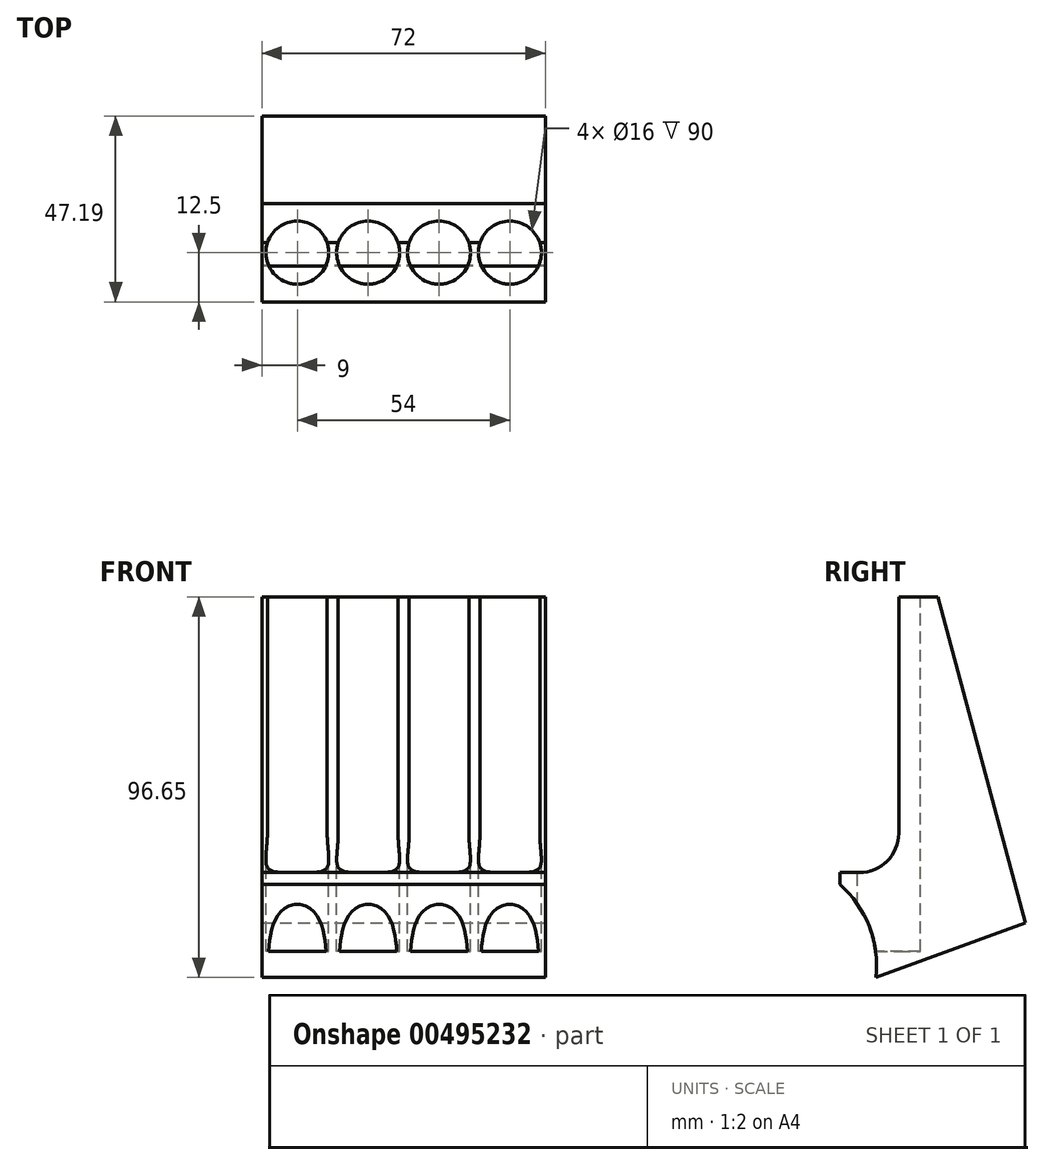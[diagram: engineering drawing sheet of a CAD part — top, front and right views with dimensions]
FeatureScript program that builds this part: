
annotation { "Feature Type Name" : "Feature", "Feature Type Description" : "" }
export const myFeature = defineFeature(function(context is Context, id is Id, definition is map)
    precondition{}
    {
        {
            var Q0;
            Q0=qCreatedBy(makeId("Front.planeOp"),FACE);
            var sketch = newSketch(context, id + "F0", { "sketchPlane" : qUnion([Q0])});
            skLineSegment(sketch, "E0.bottom", {"start": v(-36, 50) * mm, "end": v(36, 50) * mm});
            skLineSegment(sketch, "E0.top", {"start": v(-36, -50) * mm, "end": v(36, -50) * mm});
            skLineSegment(sketch, "E0.left", {"start": v(-36, 50) * mm, "end": v(-36, -50) * mm});
            skLineSegment(sketch, "E0.right", {"start": v(36, 50) * mm, "end": v(36, -50) * mm});
            skLineSegment(sketch, "E1", {"start": v(0, 50) * mm, "end": v(0, -50) * mm, "construction": true});
            skLineSegment(sketch, "E2", {"start": v(-20, 50) * mm, "end": v(-20, -50) * mm, "construction": true});
            skLineSegment(sketch, "E3", {"start": v(20, 50) * mm, "end": v(20, -50) * mm, "construction": true});
            skSolve(sketch);
        }
        {
            var Q0;
            Q0 = qSketchRegion(id + "F0", true);
            extrude(context, id + "F1", {"entities" : qUnion([Q0]), "oppositeDirection" : true, "depth" : 25 * mm, "offsetDistance" : 25 * mm});
        }
        {
            var Q0;
            Q0=makeQuery(id+"F1.opExtrude","SWEPT_FACE",FACE,{"disambiguationData":[OSD([sQuery(id+"F0.wireOp",EDGE,"E0.bottom")])]});
            var sketch = newSketch(context, id + "F2", { "sketchPlane" : qUnion([Q0])});
            skCircle(sketch, "E4", {"center": v(-27, 12.5) * mm, "radius": 8 * mm});
            skCircle(sketch, "E5", {"center": v(-9, 12.5) * mm, "radius": 8 * mm});
            skCircle(sketch, "E6", {"center": v(9, 12.5) * mm, "radius": 8 * mm});
            skCircle(sketch, "E7", {"center": v(27, 12.5) * mm, "radius": 8 * mm});
            skLineSegment(sketch, "E8", {"start": v(-36, 12.5) * mm, "end": v(36, 12.5) * mm, "construction": true});
            skSolve(sketch);
        }
        {
            var Q0;
            Q0 = qSketchRegion(id + "F2", true);
            extrude(context, id + "F3", {"entities" : qUnion([Q0]), "operationType" : NewBodyOperationType.REMOVE, "oppositeDirection" : true, "depth" : 90 * mm, "offsetDistance" : 25 * mm});
        }
        {
            var Q0;
            Q0=makeQuery(id+"F1.opExtrude","SWEPT_FACE",FACE,{"disambiguationData":[OSD([sQuery(id+"F0.wireOp",EDGE,"E0.bottom")])]});
            var sketch = newSketch(context, id + "F4", { "sketchPlane" : qUnion([Q0])});
            skLineSegment(sketch, "E9.bottom", {"start": v(-36, 0) * mm, "end": v(36, 0) * mm});
            skLineSegment(sketch, "E9.top", {"start": v(-36, 15) * mm, "end": v(36, 15) * mm});
            skLineSegment(sketch, "E9.left", {"start": v(-36, 0) * mm, "end": v(-36, 15) * mm});
            skLineSegment(sketch, "E9.right", {"start": v(36, 0) * mm, "end": v(36, 15) * mm});
            skSolve(sketch);
        }
        {
            var Q0;
            Q0 = qSketchRegion(id + "F4", true);
            extrude(context, id + "F5", {"entities" : qUnion([Q0]), "operationType" : NewBodyOperationType.REMOVE, "oppositeDirection" : true, "depth" : 70 * mm, "offsetDistance" : 25 * mm});
        }
        {
            var Q0;
            {var subQ0=sQuery(id+"F4.wireOp",EDGE,"E9.top");Q0=makeQuery(id+"F5.boolean.opBoolean","COPY",EDGE,{"disambiguationData":[TD([makeQuery(id+"F1.opExtrude","SWEPT_FACE",FACE,{"disambiguationData":[OSD([sQuery(id+"F0.wireOp",EDGE,"E0.left")])]}),makeQuery(id+"F3.boolean.opBoolean","COPY",FACE,{"derivedFrom":makeQuery(id+"F3.opExtrude","SWEPT_FACE",FACE,{"disambiguationData":[OSD([sQuery(id+"F2.wireOp",EDGE,"E4")])]})}),makeQuery(id+"F5.opExtrude","CAP_FACE",FACE,{"disambiguationData":[OSD([sQuery(id+"F4.wireOp",EDGE,"E9.bottom"),subQ0,sQuery(id+"F4.wireOp",EDGE,"E9.left"),sQuery(id+"F4.wireOp",EDGE,"E9.right")])],"isStart":false}),makeQuery(id+"F5.opExtrude","SWEPT_FACE",FACE,{"disambiguationData":[OSD([subQ0])]})])],"derivedFrom":makeQuery(id+"F5.opExtrude","CAP_EDGE",EDGE,{"disambiguationData":[OSD([subQ0])],"isStart":false})});}
            var Q1;
            {var subQ0=sQuery(id+"F4.wireOp",EDGE,"E9.top");Q1=makeQuery(id+"F5.boolean.opBoolean","COPY",EDGE,{"disambiguationData":[TD([makeQuery(id+"F3.boolean.opBoolean","COPY",FACE,{"derivedFrom":makeQuery(id+"F3.opExtrude","SWEPT_FACE",FACE,{"disambiguationData":[OSD([sQuery(id+"F2.wireOp",EDGE,"E4")])]})}),makeQuery(id+"F3.boolean.opBoolean","COPY",FACE,{"derivedFrom":makeQuery(id+"F3.opExtrude","SWEPT_FACE",FACE,{"disambiguationData":[OSD([sQuery(id+"F2.wireOp",EDGE,"E5")])]})}),makeQuery(id+"F5.opExtrude","CAP_FACE",FACE,{"disambiguationData":[OSD([sQuery(id+"F4.wireOp",EDGE,"E9.bottom"),subQ0,sQuery(id+"F4.wireOp",EDGE,"E9.left"),sQuery(id+"F4.wireOp",EDGE,"E9.right")])],"isStart":false}),makeQuery(id+"F5.opExtrude","SWEPT_FACE",FACE,{"disambiguationData":[OSD([subQ0])]})])],"derivedFrom":makeQuery(id+"F5.opExtrude","CAP_EDGE",EDGE,{"disambiguationData":[OSD([subQ0])],"isStart":false})});}
            var Q2;
            {var subQ0=sQuery(id+"F4.wireOp",EDGE,"E9.top");Q2=makeQuery(id+"F5.boolean.opBoolean","COPY",EDGE,{"disambiguationData":[TD([makeQuery(id+"F3.boolean.opBoolean","COPY",FACE,{"derivedFrom":makeQuery(id+"F3.opExtrude","SWEPT_FACE",FACE,{"disambiguationData":[OSD([sQuery(id+"F2.wireOp",EDGE,"E5")])]})}),makeQuery(id+"F3.boolean.opBoolean","COPY",FACE,{"derivedFrom":makeQuery(id+"F3.opExtrude","SWEPT_FACE",FACE,{"disambiguationData":[OSD([sQuery(id+"F2.wireOp",EDGE,"E6")])]})}),makeQuery(id+"F5.opExtrude","CAP_FACE",FACE,{"disambiguationData":[OSD([sQuery(id+"F4.wireOp",EDGE,"E9.bottom"),subQ0,sQuery(id+"F4.wireOp",EDGE,"E9.left"),sQuery(id+"F4.wireOp",EDGE,"E9.right")])],"isStart":false}),makeQuery(id+"F5.opExtrude","SWEPT_FACE",FACE,{"disambiguationData":[OSD([subQ0])]})])],"derivedFrom":makeQuery(id+"F5.opExtrude","CAP_EDGE",EDGE,{"disambiguationData":[OSD([subQ0])],"isStart":false})});}
            var Q3;
            {var subQ0=sQuery(id+"F4.wireOp",EDGE,"E9.top");Q3=makeQuery(id+"F5.boolean.opBoolean","COPY",EDGE,{"disambiguationData":[TD([makeQuery(id+"F3.boolean.opBoolean","COPY",FACE,{"derivedFrom":makeQuery(id+"F3.opExtrude","SWEPT_FACE",FACE,{"disambiguationData":[OSD([sQuery(id+"F2.wireOp",EDGE,"E6")])]})}),makeQuery(id+"F3.boolean.opBoolean","COPY",FACE,{"derivedFrom":makeQuery(id+"F3.opExtrude","SWEPT_FACE",FACE,{"disambiguationData":[OSD([sQuery(id+"F2.wireOp",EDGE,"E7")])]})}),makeQuery(id+"F5.opExtrude","CAP_FACE",FACE,{"disambiguationData":[OSD([sQuery(id+"F4.wireOp",EDGE,"E9.bottom"),subQ0,sQuery(id+"F4.wireOp",EDGE,"E9.left"),sQuery(id+"F4.wireOp",EDGE,"E9.right")])],"isStart":false}),makeQuery(id+"F5.opExtrude","SWEPT_FACE",FACE,{"disambiguationData":[OSD([subQ0])]})])],"derivedFrom":makeQuery(id+"F5.opExtrude","CAP_EDGE",EDGE,{"disambiguationData":[OSD([subQ0])],"isStart":false})});}
            var Q4;
            {var subQ0=sQuery(id+"F4.wireOp",EDGE,"E9.top");Q4=makeQuery(id+"F5.boolean.opBoolean","COPY",EDGE,{"disambiguationData":[TD([makeQuery(id+"F1.opExtrude","SWEPT_FACE",FACE,{"disambiguationData":[OSD([sQuery(id+"F0.wireOp",EDGE,"E0.right")])]}),makeQuery(id+"F3.boolean.opBoolean","COPY",FACE,{"derivedFrom":makeQuery(id+"F3.opExtrude","SWEPT_FACE",FACE,{"disambiguationData":[OSD([sQuery(id+"F2.wireOp",EDGE,"E7")])]})}),makeQuery(id+"F5.opExtrude","CAP_FACE",FACE,{"disambiguationData":[OSD([sQuery(id+"F4.wireOp",EDGE,"E9.bottom"),subQ0,sQuery(id+"F4.wireOp",EDGE,"E9.left"),sQuery(id+"F4.wireOp",EDGE,"E9.right")])],"isStart":false}),makeQuery(id+"F5.opExtrude","SWEPT_FACE",FACE,{"disambiguationData":[OSD([subQ0])]})])],"derivedFrom":makeQuery(id+"F5.opExtrude","CAP_EDGE",EDGE,{"disambiguationData":[OSD([subQ0])],"isStart":false})});}
            var Q5;
            {var subQ0=sQuery(id+"F4.wireOp",EDGE,"E9.top");Q5=makeQuery(id+"F5.boolean.opBoolean","COPY",EDGE,{"disambiguationData":[TD([makeQuery(id+"F1.opExtrude","SWEPT_FACE",FACE,{"disambiguationData":[OSD([sQuery(id+"F0.wireOp",EDGE,"E0.bottom")])]}),makeQuery(id+"F1.opExtrude","SWEPT_FACE",FACE,{"disambiguationData":[OSD([sQuery(id+"F0.wireOp",EDGE,"E0.left")])]}),makeQuery(id+"F3.boolean.opBoolean","COPY",FACE,{"derivedFrom":makeQuery(id+"F3.opExtrude","SWEPT_FACE",FACE,{"disambiguationData":[OSD([sQuery(id+"F2.wireOp",EDGE,"E4")])]})}),makeQuery(id+"F5.opExtrude","SWEPT_FACE",FACE,{"disambiguationData":[OSD([subQ0])]})])],"derivedFrom":makeQuery(id+"F5.opExtrude","CAP_EDGE",EDGE,{"disambiguationData":[OSD([subQ0])],"isStart":true})});}
            var Q6;
            {var subQ0=sQuery(id+"F4.wireOp",EDGE,"E9.top");Q6=makeQuery(id+"F5.boolean.opBoolean","COPY",EDGE,{"disambiguationData":[TD([makeQuery(id+"F1.opExtrude","SWEPT_FACE",FACE,{"disambiguationData":[OSD([sQuery(id+"F0.wireOp",EDGE,"E0.bottom")])]}),makeQuery(id+"F3.boolean.opBoolean","COPY",FACE,{"derivedFrom":makeQuery(id+"F3.opExtrude","SWEPT_FACE",FACE,{"disambiguationData":[OSD([sQuery(id+"F2.wireOp",EDGE,"E4")])]})}),makeQuery(id+"F3.boolean.opBoolean","COPY",FACE,{"derivedFrom":makeQuery(id+"F3.opExtrude","SWEPT_FACE",FACE,{"disambiguationData":[OSD([sQuery(id+"F2.wireOp",EDGE,"E5")])]})}),makeQuery(id+"F5.opExtrude","SWEPT_FACE",FACE,{"disambiguationData":[OSD([subQ0])]})])],"derivedFrom":makeQuery(id+"F5.opExtrude","CAP_EDGE",EDGE,{"disambiguationData":[OSD([subQ0])],"isStart":true})});}
            var Q7;
            {var subQ0=sQuery(id+"F4.wireOp",EDGE,"E9.top");Q7=makeQuery(id+"F5.boolean.opBoolean","COPY",EDGE,{"disambiguationData":[TD([makeQuery(id+"F1.opExtrude","SWEPT_FACE",FACE,{"disambiguationData":[OSD([sQuery(id+"F0.wireOp",EDGE,"E0.bottom")])]}),makeQuery(id+"F3.boolean.opBoolean","COPY",FACE,{"derivedFrom":makeQuery(id+"F3.opExtrude","SWEPT_FACE",FACE,{"disambiguationData":[OSD([sQuery(id+"F2.wireOp",EDGE,"E5")])]})}),makeQuery(id+"F3.boolean.opBoolean","COPY",FACE,{"derivedFrom":makeQuery(id+"F3.opExtrude","SWEPT_FACE",FACE,{"disambiguationData":[OSD([sQuery(id+"F2.wireOp",EDGE,"E6")])]})}),makeQuery(id+"F5.opExtrude","SWEPT_FACE",FACE,{"disambiguationData":[OSD([subQ0])]})])],"derivedFrom":makeQuery(id+"F5.opExtrude","CAP_EDGE",EDGE,{"disambiguationData":[OSD([subQ0])],"isStart":true})});}
            var Q8;
            {var subQ0=sQuery(id+"F4.wireOp",EDGE,"E9.top");Q8=makeQuery(id+"F5.boolean.opBoolean","COPY",EDGE,{"disambiguationData":[TD([makeQuery(id+"F1.opExtrude","SWEPT_FACE",FACE,{"disambiguationData":[OSD([sQuery(id+"F0.wireOp",EDGE,"E0.bottom")])]}),makeQuery(id+"F3.boolean.opBoolean","COPY",FACE,{"derivedFrom":makeQuery(id+"F3.opExtrude","SWEPT_FACE",FACE,{"disambiguationData":[OSD([sQuery(id+"F2.wireOp",EDGE,"E6")])]})}),makeQuery(id+"F3.boolean.opBoolean","COPY",FACE,{"derivedFrom":makeQuery(id+"F3.opExtrude","SWEPT_FACE",FACE,{"disambiguationData":[OSD([sQuery(id+"F2.wireOp",EDGE,"E7")])]})}),makeQuery(id+"F5.opExtrude","SWEPT_FACE",FACE,{"disambiguationData":[OSD([subQ0])]})])],"derivedFrom":makeQuery(id+"F5.opExtrude","CAP_EDGE",EDGE,{"disambiguationData":[OSD([subQ0])],"isStart":true})});}
            var Q9;
            {var subQ0=sQuery(id+"F4.wireOp",EDGE,"E9.top");Q9=makeQuery(id+"F5.boolean.opBoolean","COPY",EDGE,{"disambiguationData":[TD([makeQuery(id+"F1.opExtrude","SWEPT_FACE",FACE,{"disambiguationData":[OSD([sQuery(id+"F0.wireOp",EDGE,"E0.bottom")])]}),makeQuery(id+"F1.opExtrude","SWEPT_FACE",FACE,{"disambiguationData":[OSD([sQuery(id+"F0.wireOp",EDGE,"E0.right")])]}),makeQuery(id+"F3.boolean.opBoolean","COPY",FACE,{"derivedFrom":makeQuery(id+"F3.opExtrude","SWEPT_FACE",FACE,{"disambiguationData":[OSD([sQuery(id+"F2.wireOp",EDGE,"E7")])]})}),makeQuery(id+"F5.opExtrude","SWEPT_FACE",FACE,{"disambiguationData":[OSD([subQ0])]})])],"derivedFrom":makeQuery(id+"F5.opExtrude","CAP_EDGE",EDGE,{"disambiguationData":[OSD([subQ0])],"isStart":true})});}
            fillet(context, id + "F6", {"entities" : qUnion([Q0, Q1, Q2, Q3, Q4, Q5, Q6, Q7, Q8, Q9]), "radius" : 10 * mm, "tangentPropagation" : true, "allowEdgeOverflow" : false});
        }
        {
            var Q0;
            Q0=makeQuery(id+"F1.opExtrude","SWEPT_FACE",FACE,{"disambiguationData":[OSD([sQuery(id+"F0.wireOp",EDGE,"E0.right")])]});
            var sketch = newSketch(context, id + "F7", { "sketchPlane" : qUnion([Q0])});
            skLineSegment(sketch, "E10", {"start": v(0, -50) * mm, "end": v(25, -40.9) * mm});
            skLineSegment(sketch, "E11", {"start": v(25, -40.9) * mm, "end": v(25, -50) * mm});
            skLineSegment(sketch, "E12", {"start": v(25, -50) * mm, "end": v(0, -50) * mm});
            skSolve(sketch);
        }
        {
            var Q0;
            Q0 = qSketchRegion(id + "F7", true);
            extrude(context, id + "F8", {"entities" : qUnion([Q0]), "operationType" : NewBodyOperationType.REMOVE, "endBound" : BoundingType.THROUGH_ALL, "oppositeDirection" : true, "depth" : 72 * mm, "offsetDistance" : 25 * mm});
        }
        {
            var Q0;
            Q0=makeQuery(id+"F8.boolean.opBoolean","MERGE",FACE,{"derivedFrom":[makeQuery(id+"F1.opExtrude","SWEPT_FACE",FACE,{"disambiguationData":[OSD([sQuery(id+"F0.wireOp",EDGE,"E0.right")])]}),makeQuery(id+"F8.opExtrude","CAP_FACE",FACE,{"disambiguationData":[OSD([sQuery(id+"F7.wireOp",EDGE,"gOEuhXYe-nncB-Ul7h-NU9X-Q1V6e6p96okb"),sQuery(id+"F7.wireOp",EDGE,"V4sgcEXz-Ydqn-Qiog-50gN-6tMW1AEewKdl"),sQuery(id+"F7.wireOp",EDGE,"i34p7GkN-Z38o-gXI6-Lqds-SdKWRN6jjZfa")])],"isStart":true})]});
            var sketch = newSketch(context, id + "F9", { "sketchPlane" : qUnion([Q0])});
            skLineSegment(sketch, "E13", {"start": v(9.2, -46.65) * mm, "end": v(0, -50) * mm});
            skLineSegment(sketch, "E14", {"start": v(0, -50) * mm, "end": v(0, -23) * mm});
            skArc(sketch, "E15", {"start": v(9.2, -46.65) * mm, "mid": v(7.5, -33.7) * mm, "end": v(0, -23) * mm});
            skSolve(sketch);
        }
        {
            var Q0;
            Q0 = qSketchRegion(id + "F9", true);
            extrude(context, id + "F10", {"entities" : qUnion([Q0]), "operationType" : NewBodyOperationType.REMOVE, "endBound" : BoundingType.THROUGH_ALL, "oppositeDirection" : true, "depth" : 25 * mm, "offsetDistance" : 25 * mm});
        }
        {
            var Q0;
            Q0=makeQuery(id+"F1.opExtrude","SWEPT_FACE",FACE,{"disambiguationData":[OSD([sQuery(id+"F0.wireOp",EDGE,"E0.right")])]});
            var sketch = newSketch(context, id + "F11", { "sketchPlane" : qUnion([Q0])});
            skLineSegment(sketch, "E16", {"start": v(25, -40.9) * mm, "end": v(47.2, -32.82) * mm});
            skLineSegment(sketch, "E17", {"start": v(47.2, -32.82) * mm, "end": v(25, 50) * mm});
            skLineSegment(sketch, "E18", {"start": v(25, 50) * mm, "end": v(25, -40.9) * mm});
            skSolve(sketch);
        }
        {
            var Q0;
            Q0 = qSketchRegion(id + "F11", true);
            extrude(context, id + "F12", {"entities" : qUnion([Q0]), "operationType" : NewBodyOperationType.ADD, "oppositeDirection" : true, "depth" : 72 * mm, "offsetDistance" : 25 * mm});
        }
    });
